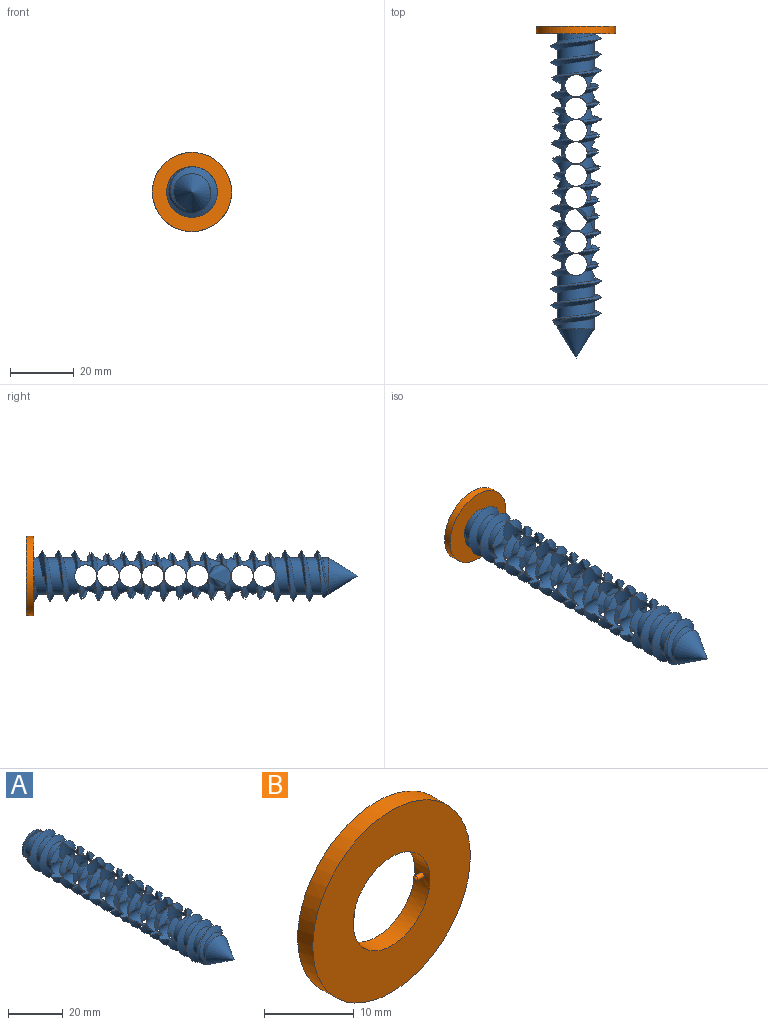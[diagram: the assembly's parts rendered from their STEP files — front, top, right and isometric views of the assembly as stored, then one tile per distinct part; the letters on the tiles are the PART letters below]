
ASSEMBLY  parts=2 mates=1
PART A: 217 faces, bbox 16.7x105x19.1 mm
  f0: cylinder r=5.74mm len=11.48mm, axis (0,-1,0), area 110mm2, adj f1,f207,f208,f209,f210,f211,f212
  f1: bspline ~18.33x15.88mm, area 173.4mm2, adj f0,f2,f205,f206,f207,f208,f210,f211
  f2: bspline ~11.91x9.17mm, area 14.2mm2, adj f1,f3,f205,f206
  f3: cylinder r=5.74mm len=3.63mm, axis (0,-1,0), area 6mm2, adj f2,f4,f205,f206
  f4: bspline ~11.91x9.17mm, area 4.3mm2, adj f3,f5,f205,f206
  f5: bspline ~11.91x9.17mm, area 6.7mm2, adj f4,f6,f205,f206
  f6: bspline ~18.33x11.91mm, area 39.1mm2, adj f5,f7,f201,f202,f203,f204,f205,f206
  f7: cylinder r=5.74mm len=11.48mm, axis (0,-1,0), area 51.7mm2, adj f6,f8,f17,f18,f19,f20,f21,f196
  f8: cylinder r=3.49mm len=7.16mm, axis (1,0,0), area 70.2mm2, adj f7,f9,f10,f11,f14,f15,f16,f17
  f9: bspline ~11.91x9.17mm, area 5.2mm2, adj f8,f10,f17,f18
  f10: bspline ~11.91x9.17mm, area 3.4mm2, adj f8,f9,f11,f18
  f11: cylinder r=5.74mm len=11.48mm, axis (0,-1,0), area 101.7mm2, adj f8,f10,f12,f18,f206,f208,f209,f210
  f12: bspline ~11.91x9.17mm, area 5.3mm2, adj f11,f13,f18,f206
  f13: bspline ~11.91x9.17mm, area 6.6mm2, adj f12,f18,f19,f206
  f14: cylinder r=5.74mm len=4.31mm, axis (0,-1,0), area 8.2mm2, adj f8,f15,f205,f210
  f15: bspline ~11.91x9.17mm, area 3.1mm2, adj f8,f14,f16,f205
  f16: bspline ~11.91x9.17mm, area 5.2mm2, adj f8,f15,f200,f205
  f17: bspline ~11.91x9.17mm, area 8.8mm2, adj f7,f8,f9,f18
  f18: cylinder r=3.49mm len=7.25mm, axis (0,0,1), area 70.1mm2, adj f7,f8,f9,f10,f11,f12,f13,f17
  f19: bspline ~11.91x9.17mm, area 9.3mm2, adj f7,f13,f18,f206
  f20: bspline ~11.91x9.17mm, area 9mm2, adj f7,f201,f202,f206
  f21: bspline ~11.91x9.17mm, area 7.7mm2, adj f7,f22,f196,f202
  f22: bspline ~11.91x9.17mm, area 8.3mm2, adj f21,f23,f196,f202
  f23: bspline ~11.91x9.17mm, area 11mm2, adj f22,f24,f196,f202
  f24: cylinder r=5.74mm len=3.68mm, axis (0,-1,0), area 6.5mm2, adj f23,f25,f196,f202
  f25: bspline ~11.91x9.17mm, area 5.6mm2, adj f24,f26,f196,f202
  f26: bspline ~11.91x9.17mm, area 8.3mm2, adj f25,f27,f196,f202
  f27: bspline ~18.33x11.91mm, area 34.7mm2, adj f26,f28,f30,f186,f187,f188,f196,f202
  f28: bspline ~11.91x9.17mm, area 9.9mm2, adj f27,f29,f30,f196
  f29: bspline ~11.91x9.17mm, area 8.1mm2, adj f28,f30,f188,f196
  f30: cylinder r=3.49mm len=7.73mm, axis (0,0,1), area 81.2mm2, adj f27,f28,f29,f31,f177,f178,f179,f180
  f31: cylinder r=3.49mm len=7.25mm, axis (1,0,0), area 70.7mm2, adj f30,f32,f33,f173,f174,f175,f176,f177
  f32: bspline ~11.91x9.17mm, area 8.8mm2, adj f31,f33,f175,f176
  f33: cylinder r=5.74mm len=11.48mm, axis (0,-1,0), area 40.3mm2, adj f31,f32,f34,f164,f165,f166,f169,f170
  f34: cylinder r=3.49mm len=7.17mm, axis (1,0,0), area 70.1mm2, adj f33,f35,f36,f37,f38,f39,f164,f165
  f35: bspline ~11.91x9.17mm, area 8.7mm2, adj f34,f36,f39,f171
  f36: bspline ~11.91x9.17mm, area 5.8mm2, adj f34,f35,f171,f172
  f37: bspline ~11.91x9.17mm, area 5.1mm2, adj f34,f38,f164,f165
  f38: bspline ~11.91x9.17mm, area 9.5mm2, adj f34,f37,f39,f165
  f39: cylinder r=5.74mm len=11.48mm, axis (0,-1,0), area 48.7mm2, adj f34,f35,f38,f40,f42,f148,f149,f150
  f40: bspline ~11.91x9.17mm, area 8.1mm2, adj f39,f41,f42,f171
  f41: bspline ~11.91x9.17mm, area 9.8mm2, adj f40,f42,f154,f171
  f42: cylinder r=3.49mm len=7.71mm, axis (1,0,0), area 82.8mm2, adj f39,f40,f41,f43,f44,f45,f46,f47
  f43: bspline ~11.91x9.17mm, area 6.8mm2, adj f42,f44,f148,f149
  f44: bspline ~11.91x9.17mm, area 9.5mm2, adj f42,f43,f45,f149
  f45: cylinder r=5.74mm len=4.02mm, axis (0,-1,0), area 7.9mm2, adj f42,f44,f46,f149
  f46: bspline ~11.91x9.17mm, area 7.7mm2, adj f42,f45,f47,f149
  f47: bspline ~15.88x9.17mm, area 18.4mm2, adj f42,f46,f48,f141,f142,f143,f144,f149
  f48: bspline ~11.91x9.17mm, area 11.3mm2, adj f47,f49,f141,f143
  f49: cylinder r=5.74mm len=3.66mm, axis (0,-1,0), area 6.4mm2, adj f48,f50,f141,f143
  f50: bspline ~11.91x9.17mm, area 5.3mm2, adj f49,f51,f141,f143
  f51: bspline ~11.91x9.17mm, area 7.9mm2, adj f50,f52,f141,f143
  f52: bspline ~18.33x11.91mm, area 35.2mm2, adj f51,f53,f55,f121,f122,f123,f141,f143
  f53: bspline ~11.91x9.17mm, area 9.7mm2, adj f52,f54,f55,f143
  f54: bspline ~11.91x9.17mm, area 8.1mm2, adj f53,f55,f123,f143
  f55: cylinder r=3.49mm len=7.7mm, axis (0,0,1), area 80.4mm2, adj f52,f53,f54,f56,f57,f112,f113,f114
  f56: bspline ~11.91x9.17mm, area 7.5mm2, adj f55,f57,f118,f119
  f57: bspline ~18.33x11.91mm, area 18.8mm2, adj f55,f56,f58,f109,f110,f111,f112,f119
  f58: bspline ~11.91x9.17mm, area 8.8mm2, adj f57,f59,f109,f119
  f59: cylinder r=5.74mm len=11.46mm, axis (0,-1,0), area 43.5mm2, adj f58,f60,f63,f66,f67,f106,f107,f108
  f60: bspline ~11.91x9.17mm, area 11mm2, adj f59,f61,f63,f122
  f61: bspline ~11.91x9.17mm, area 5.2mm2, adj f60,f62,f63,f122
  f62: bspline ~6.87x5.07mm, area 3.1mm2, adj f61,f63,f122,f123
  f63: cylinder r=3.49mm len=7.15mm, axis (0,0,1), area 70.2mm2, adj f59,f60,f61,f62,f64,f65,f66,f119
  f64: bspline ~11.91x9.17mm, area 5.3mm2, adj f63,f65,f66,f119
  f65: bspline ~11.91x9.17mm, area 3.6mm2, adj f63,f64,f119,f123
  f66: bspline ~11.91x9.17mm, area 8.7mm2, adj f59,f63,f64,f119
  f67: bspline ~11.91x9.17mm, area 4.4mm2, adj f59,f68,f106,f109
  f68: bspline ~11.91x9.17mm, area 5.9mm2, adj f67,f69,f106,f109
  f69: bspline ~11.91x9.17mm, area 8.8mm2, adj f68,f70,f106,f109
  f70: cylinder r=5.74mm len=11.48mm, axis (0,-1,0), area 51.8mm2, adj f69,f71,f89,f90,f91,f92,f93,f94
  f71: cylinder r=3.49mm len=7.68mm, axis (1,0,0), area 82.5mm2, adj f70,f72,f73,f74,f82,f83,f84,f85
  f72: cylinder r=5.74mm len=3.76mm, axis (0,-1,0), area 7.6mm2, adj f71,f73,f88,f90
  f73: bspline ~11.91x9.17mm, area 7.1mm2, adj f71,f72,f74,f90
  f74: bspline ~18.33x18.2mm, area 155mm2, adj f71,f73,f75,f81,f82,f90
  f75: bspline ~18.33x17.78mm, area 151.2mm2, adj f74,f76,f81,f90
  f76: cylinder r=5.74mm len=19.52mm, axis (0,-1,0), area 408.2mm2, adj f75,f77,f79,f81,f82,f90,f92,f94
  f77: bspline ~11.91x9.17mm, area 8.7mm2, adj f76,f78,f90,f92
  f78: bspline ~11.91x9.17mm, area 5.3mm2, adj f77,f90,f91,f92
  f79: bspline ~11.91x9.17mm, area 10.8mm2, adj f76,f80,f92,f94
  f80: bspline ~11.91x9.17mm, area 5.1mm2, adj f79,f92,f93,f94
  f81: cone r=7.94mm half-angle=32deg, axis (0,1,0), area 231.2mm2, adj f74,f75,f76,f82
  f82: bspline ~19.9x18.33mm, area 339.3mm2, adj f71,f74,f76,f81,f83,f94
  f83: bspline ~11.91x9.17mm, area 6.3mm2, adj f71,f82,f84,f94
  f84: bspline ~11.91x9.17mm, area 4mm2, adj f71,f83,f85,f94
  f85: cylinder r=5.74mm len=3.63mm, axis (0,-1,0), area 6mm2, adj f71,f84,f94,f95
  f86: bspline ~11.91x9.17mm, area 9.6mm2, adj f71,f95,f105,f109
  f87: bspline ~11.91x9.17mm, area 7mm2, adj f71,f88,f89,f90
  f88: bspline ~11.91x9.17mm, area 9.7mm2, adj f71,f72,f87,f90
  f89: bspline ~11.91x9.17mm, area 5.9mm2, adj f70,f71,f87,f90
  f90: cylinder r=3.49mm len=7.28mm, axis (0,0,1), area 74.9mm2, adj f70,f71,f72,f73,f74,f75,f76,f77
  f91: bspline ~11.91x9.17mm, area 3.6mm2, adj f70,f78,f90,f92
  f92: cylinder r=3.49mm len=7.14mm, axis (1,0,0), area 70.1mm2, adj f70,f76,f77,f78,f79,f80,f90,f91
  f93: bspline ~11.91x9.17mm, area 2.6mm2, adj f70,f80,f92,f94
  f94: cylinder r=3.49mm len=7.62mm, axis (0,0,1), area 109.6mm2, adj f70,f71,f76,f79,f80,f82,f83,f84
  f95: bspline ~15.88x9.17mm, area 35.6mm2, adj f70,f71,f85,f86,f94,f96,f109,f111
  f96: bspline ~11.91x9.17mm, area 7.7mm2, adj f95,f97,f109,f111
  f97: bspline ~11.91x9.17mm, area 5.2mm2, adj f96,f98,f109,f111
  f98: cylinder r=5.74mm len=3.64mm, axis (0,-1,0), area 6.3mm2, adj f97,f109,f110,f111
  f99: bspline ~11.91x9.17mm, area 13.7mm2, adj f70,f100,f108,f111
  f100: bspline ~11.91x9.17mm, area 5.6mm2, adj f99,f101,f108,f111
  f101: bspline ~11.91x9.17mm, area 3.4mm2, adj f100,f102,f108,f111
  f102: cylinder r=5.74mm len=3.68mm, axis (0,-1,0), area 6.7mm2, adj f101,f108,f111,f112
  f103: bspline ~11.91x9.17mm, area 9.4mm2, adj f70,f104,f106,f108
  f104: bspline ~11.91x9.17mm, area 5.1mm2, adj f103,f106,f107,f108
  f105: bspline ~11.91x9.17mm, area 8.2mm2, adj f70,f71,f86,f109
  f106: cylinder r=3.49mm len=7.18mm, axis (1,0,0), area 70.1mm2, adj f59,f67,f68,f69,f70,f103,f104,f107
  f107: bspline ~6.87x5.07mm, area 3.2mm2, adj f59,f104,f106,f108
  f108: cylinder r=3.49mm len=7.22mm, axis (0,0,1), area 72.4mm2, adj f59,f70,f99,f100,f101,f102,f103,f104
  f109: cylinder r=3.49mm len=7.9mm, axis (0,0,1), area 81.9mm2, adj f57,f58,f59,f67,f68,f69,f70,f86
  f110: bspline ~11.91x9.17mm, area 11.6mm2, adj f57,f98,f109,f111
  f111: cylinder r=3.49mm len=7.8mm, axis (1,0,0), area 81.8mm2, adj f57,f70,f95,f96,f97,f98,f99,f100
  f112: bspline ~15.32x6.89mm, area 37.7mm2, adj f55,f57,f59,f102,f108,f111,f113,f122
  f113: bspline ~11.91x9.17mm, area 6.4mm2, adj f55,f112,f114,f122
  f114: bspline ~11.91x9.17mm, area 4.1mm2, adj f55,f113,f121,f122
  f115: bspline ~11.91x9.17mm, area 5.7mm2, adj f55,f116,f119,f123
  f116: bspline ~11.91x9.17mm, area 6.9mm2, adj f55,f115,f117,f119
  f117: bspline ~11.91x9.17mm, area 9.6mm2, adj f55,f116,f118,f119
  f118: cylinder r=5.74mm len=3.85mm, axis (0,-1,0), area 7.8mm2, adj f55,f56,f117,f119
  f119: cylinder r=3.49mm len=7.27mm, axis (1,0,0), area 185.2mm2, adj f55,f56,f57,f58,f59,f63,f64,f65
  f120: cylinder r=5.74mm len=6.99mm, axis (0,-1,0), area 40.4mm2, adj f119
  f121: cylinder r=5.74mm len=3.63mm, axis (0,-1,0), area 6mm2, adj f52,f55,f114,f122
  f122: cylinder r=3.49mm len=7.7mm, axis (1,0,0), area 78.3mm2, adj f52,f55,f59,f60,f61,f62,f63,f112
  f123: cylinder r=5.74mm len=11.48mm, axis (0,-1,0), area 51.7mm2, adj f52,f54,f55,f62,f63,f65,f115,f119
  f124: bspline ~11.91x9.17mm, area 14mm2, adj f123,f125,f128,f141
  f125: bspline ~11.91x9.17mm, area 5.6mm2, adj f124,f126,f128,f141
  f126: bspline ~11.91x9.17mm, area 3.4mm2, adj f125,f127,f128,f141
  f127: cylinder r=5.74mm len=3.69mm, axis (0,-1,0), area 6.7mm2, adj f126,f128,f141,f144
  f128: cylinder r=3.49mm len=7.22mm, axis (1,0,0), area 72.7mm2, adj f123,f124,f125,f126,f127,f129,f130,f137
  f129: bspline ~11.91x9.17mm, area 3.1mm2, adj f128,f130,f137,f139
  f130: cylinder r=5.74mm len=11.47mm, axis (0,-1,0), area 45.9mm2, adj f128,f129,f131,f133,f135,f139,f142,f143
  f131: bspline ~11.91x9.17mm, area 11.1mm2, adj f130,f132,f151,f153
  f132: bspline ~11.91x9.17mm, area 5.2mm2, adj f131,f151,f152,f153
  f133: bspline ~11.91x9.17mm, area 8.7mm2, adj f130,f134,f149,f151
  f134: bspline ~11.91x9.17mm, area 5.3mm2, adj f133,f149,f150,f151
  f135: bspline ~11.91x9.17mm, area 4.3mm2, adj f130,f136,f139,f143
  f136: bspline ~11.91x9.17mm, area 5.8mm2, adj f135,f139,f140,f143
  f137: bspline ~11.91x9.17mm, area 5.1mm2, adj f128,f129,f138,f139
  f138: bspline ~11.91x9.17mm, area 9.4mm2, adj f123,f128,f137,f139
  f139: cylinder r=3.49mm len=7.17mm, axis (0,0,1), area 70.1mm2, adj f123,f128,f129,f130,f135,f136,f137,f138
  f140: bspline ~11.91x9.17mm, area 8.7mm2, adj f123,f136,f139,f143
  f141: cylinder r=3.49mm len=7.79mm, axis (0,0,1), area 84.7mm2, adj f47,f48,f49,f50,f51,f52,f123,f124
  f142: bspline ~11.91x9.17mm, area 9mm2, adj f47,f130,f143,f149
  f143: cylinder r=3.49mm len=7.91mm, axis (1,0,0), area 80.2mm2, adj f47,f48,f49,f50,f51,f52,f53,f54
  f144: bspline ~18.33x11.91mm, area 38.2mm2, adj f42,f47,f127,f128,f130,f141,f145,f153
  f145: bspline ~11.91x9.17mm, area 6.5mm2, adj f42,f144,f146,f153
  f146: bspline ~11.91x9.17mm, area 4.2mm2, adj f42,f145,f147,f153
  f147: cylinder r=5.74mm len=3.63mm, axis (0,-1,0), area 6mm2, adj f42,f146,f153,f154
  f148: bspline ~11.91x9.17mm, area 5.6mm2, adj f39,f42,f43,f149
  f149: cylinder r=3.49mm len=7.26mm, axis (0,0,1), area 72mm2, adj f39,f42,f43,f44,f45,f46,f47,f130
  f150: bspline ~11.91x9.17mm, area 3.5mm2, adj f39,f134,f149,f151
  f151: cylinder r=3.49mm len=7.15mm, axis (1,0,0), area 70.1mm2, adj f39,f130,f131,f132,f133,f134,f149,f150
  f152: bspline ~11.91x9.17mm, area 3.1mm2, adj f39,f132,f151,f153
  f153: cylinder r=3.49mm len=7.79mm, axis (0,0,1), area 78.9mm2, adj f39,f42,f130,f131,f132,f144,f145,f146
  f154: bspline ~15.88x9.17mm, area 34.9mm2, adj f39,f41,f42,f147,f153,f155,f169,f171
  f155: bspline ~11.91x9.17mm, area 8mm2, adj f154,f156,f169,f171
  f156: bspline ~11.91x9.17mm, area 5.5mm2, adj f155,f157,f169,f171
  f157: cylinder r=5.74mm len=3.65mm, axis (0,-1,0), area 6.4mm2, adj f156,f158,f169,f171
  f158: bspline ~11.91x9.17mm, area 11.2mm2, adj f157,f159,f169,f171
  f159: bspline ~11.91x9.17mm, area 8.7mm2, adj f158,f169,f170,f171
  f160: bspline ~11.91x9.17mm, area 14.5mm2, adj f39,f161,f165,f169
  f161: bspline ~11.91x9.17mm, area 5.7mm2, adj f160,f162,f165,f169
  f162: bspline ~11.91x9.17mm, area 3.5mm2, adj f161,f163,f165,f169
  f163: cylinder r=5.74mm len=3.66mm, axis (0,-1,0), area 6.5mm2, adj f162,f165,f169,f183
  f164: bspline ~6.87x5.07mm, area 3.1mm2, adj f33,f34,f37,f165
  f165: cylinder r=3.49mm len=7.23mm, axis (0,0,1), area 74.1mm2, adj f33,f34,f37,f38,f39,f160,f161,f162
  f166: bspline ~11.91x9.17mm, area 11.3mm2, adj f33,f167,f176,f187
  f167: bspline ~11.91x9.17mm, area 5.2mm2, adj f166,f168,f176,f187
  f168: bspline ~6.87x5.07mm, area 2.6mm2, adj f167,f176,f187,f188
  f169: cylinder r=3.49mm len=7.77mm, axis (1,0,0), area 84.5mm2, adj f33,f39,f154,f155,f156,f157,f158,f159
  f170: bspline ~11.91x9.17mm, area 8.3mm2, adj f33,f159,f169,f171
  f171: cylinder r=3.49mm len=7.93mm, axis (0,0,1), area 78.6mm2, adj f33,f34,f35,f36,f39,f40,f41,f154
  f172: bspline ~11.91x9.17mm, area 4.2mm2, adj f33,f34,f36,f171
  f173: bspline ~13.75x5.07mm, area 0.3mm2, adj f31,f33,f169,f182
  f174: bspline ~11.91x9.17mm, area 3.5mm2, adj f31,f175,f176,f188
  f175: bspline ~11.91x9.17mm, area 5.2mm2, adj f31,f32,f174,f176
  f176: cylinder r=3.49mm len=7.16mm, axis (0,0,1), area 70.2mm2, adj f31,f32,f33,f166,f167,f168,f174,f175
  f177: bspline ~11.91x9.17mm, area 5.4mm2, adj f30,f31,f178,f188
  f178: bspline ~11.91x9.17mm, area 6.7mm2, adj f30,f31,f177,f179
  f179: bspline ~11.91x9.17mm, area 9.4mm2, adj f30,f31,f178,f180
  f180: cylinder r=5.74mm len=4.47mm, axis (0,-1,0), area 8.2mm2, adj f30,f31,f179,f181
  f181: bspline ~11.91x9.17mm, area 8.4mm2, adj f30,f31,f180,f182
  f182: bspline ~16.04x11.91mm, area 9.8mm2, adj f30,f31,f169,f173,f181,f183
  f183: bspline ~15.35x6.76mm, area 38.6mm2, adj f30,f33,f163,f165,f169,f182,f184,f187
  f184: bspline ~11.91x9.17mm, area 6.5mm2, adj f30,f183,f185,f187
  f185: bspline ~11.91x9.17mm, area 4.3mm2, adj f30,f184,f186,f187
  f186: cylinder r=5.74mm len=3.63mm, axis (0,-1,0), area 6mm2, adj f27,f30,f185,f187
  f187: cylinder r=3.49mm len=7.87mm, axis (1,0,0), area 111.8mm2, adj f27,f30,f33,f166,f167,f168,f176,f183
  f188: cylinder r=5.74mm len=11.48mm, axis (0,-1,0), area 48.6mm2, adj f27,f29,f30,f31,f168,f174,f176,f177
  f189: bspline ~11.91x9.17mm, area 14.8mm2, adj f188,f190,f202,f204
  f190: bspline ~11.91x9.17mm, area 5.7mm2, adj f189,f191,f202,f204
  f191: bspline ~11.91x9.17mm, area 3.5mm2, adj f190,f202,f203,f204
  f192: bspline ~11.91x9.17mm, area 9.6mm2, adj f188,f193,f198,f204
  f193: bspline ~11.91x9.17mm, area 5.1mm2, adj f192,f198,f199,f204
  f194: bspline ~11.91x9.17mm, area 8.7mm2, adj f188,f195,f196,f198
  f195: bspline ~11.91x9.17mm, area 5.7mm2, adj f194,f196,f197,f198
  f196: cylinder r=3.49mm len=7.94mm, axis (1,0,0), area 80.4mm2, adj f7,f21,f22,f23,f24,f25,f26,f27
  f197: bspline ~11.91x9.17mm, area 4.2mm2, adj f7,f195,f196,f198
  f198: cylinder r=3.49mm len=7.16mm, axis (0,0,1), area 70.1mm2, adj f7,f188,f192,f193,f194,f195,f196,f197
  f199: bspline ~11.91x9.17mm, area 3.1mm2, adj f7,f193,f198,f204
  f200: bspline ~11.91x9.17mm, area 11.5mm2, adj f7,f8,f16,f205
  f201: bspline ~11.91x9.17mm, area 9.9mm2, adj f6,f20,f202,f206
  f202: cylinder r=3.49mm len=7.76mm, axis (0,0,1), area 80.6mm2, adj f6,f7,f20,f21,f22,f23,f24,f25
  f203: cylinder r=5.74mm len=3.68mm, axis (0,-1,0), area 6.5mm2, adj f6,f191,f202,f204
  f204: cylinder r=3.49mm len=7.24mm, axis (1,0,0), area 73.5mm2, adj f6,f7,f188,f189,f190,f191,f192,f193
  f205: cylinder r=3.49mm len=7.94mm, axis (0,0,1), area 79.4mm2, adj f1,f2,f3,f4,f5,f6,f7,f8
  f206: cylinder r=3.49mm len=7.74mm, axis (1,0,0), area 80.3mm2, adj f1,f2,f3,f4,f5,f6,f7,f11
  f207: plane 1.22x0.7mm, normal (0,0,-1), area 0.4mm2, adj f0,f1,f208
  f208: bspline ~18.33x15.88mm, area 95.5mm2, adj f0,f1,f11,f206,f207,f209
  f209: cylinder r=5.74mm len=11.48mm, axis (0,-1,0), area 116.8mm2, adj f0,f11,f208,f210
  f210: bspline ~18.33x15.88mm, area 283.7mm2, adj f0,f1,f8,f11,f14,f205,f209,f211
  f211: plane 12.59x8.75mm, normal (0,1,0), area 22.3mm2, adj f0,f1,f210
  f212: plane 11.48x11.48mm, normal (0,1,0), area 40.7mm2, adj f0,f213
  f213: cylinder r=4.47mm len=8.94mm, axis (0,1,0), area 26.7mm2, adj f212,f214
  f214: plane 11.48x11.48mm, normal (0,-1,0), area 40.7mm2, adj f213,f215
  f215: cylinder r=5.74mm len=11.48mm, axis (0,-1,0), area 28.6mm2, adj f214,f216
  f216: plane 11.48x11.48mm, normal (0,1,0), area 103.4mm2, adj f215
PART B: 10 faces, bbox 24.8x2.4x24.8 mm
  f0: cylinder r=6.06mm len=12.11mm, axis (0,1,0), area 90mm2, adj f1,f2,f4,f7
  f1: plane 24.81x24.81mm, normal (0,-1,0), area 368.3mm2, adj f0,f3
  f2: plane 24.81x24.81mm, normal (0,1,0), area 368.3mm2, adj f0,f3
  f3: cylinder r=12.41mm len=24.81mm, axis (0,1,0), area 185.6mm2, adj f1,f2
  f4: cylinder r=0.32mm len=1.02mm, axis (1,0,0), area 2mm2, adj f0,f6
  f5: plane 0.13x0.13mm, normal (-1,0,0), area 0mm2, adj f6
  f6: torus R=0.06mm, axis (1,0,0), area 0.6mm2, adj f4,f5
  f7: cylinder r=0.32mm len=1.02mm, axis (-1,0,0), area 2mm2, adj f0,f9
  f8: plane 0.13x0.13mm, normal (1,0,0), area 0mm2, adj f9
  f9: torus R=0.06mm, axis (1,0,0), area 0.6mm2, adj f7,f8
PLACE A t=(-44.11,31.13,-32.7)mm fixed
PLACE B rot(axis=(0,1,0),55.2deg) t=(-44.11,31.13,-32.7)mm
MATE revolute A.f0 <-> B.f3  axis (0,1,0) through (-44.11,33.67,-32.7)mm
